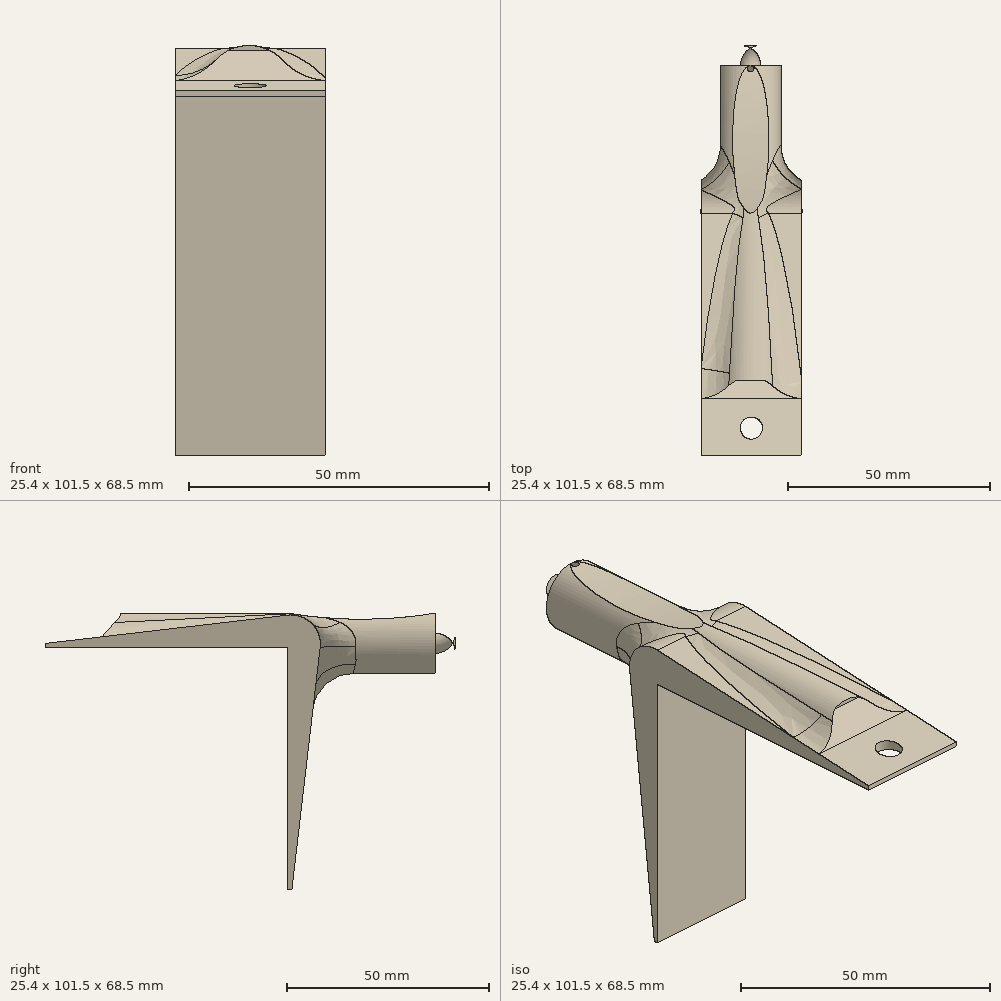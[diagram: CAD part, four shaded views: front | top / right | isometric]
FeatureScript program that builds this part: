
annotation { "Feature Type Name" : "Feature", "Feature Type Description" : "" }
export const myFeature = defineFeature(function(context is Context, id is Id, definition is map)
    precondition{}
    {
        {
            var Q0;
            Q0=qCreatedBy(makeId("Right.planeOp"),FACE);
            var sketch = newSketch(context, id + "F0", { "sketchPlane" : qUnion([Q0])});
            skLineSegment(sketch, "E0", {"start": v(0, 0) * mm, "end": v(0, -60) * mm});
            skLineSegment(sketch, "E1", {"start": v(0, 0) * mm, "end": v(-60, 0) * mm});
            skLineSegment(sketch, "E2", {"start": v(0, 0) * mm, "end": v(0, 8) * mm, "construction": true});
            skLineSegment(sketch, "E3", {"start": v(0, 0) * mm, "end": v(8, 0) * mm, "construction": true});
            skLineSegment(sketch, "E4", {"start": v(-60, 0) * mm, "end": v(-60, 1) * mm});
            skLineSegment(sketch, "E5", {"start": v(0, -60) * mm, "end": v(1, -60) * mm});
            skLineSegment(sketch, "E6", {"start": v(-60, 1) * mm, "end": v(0, 8) * mm});
            skLineSegment(sketch, "E7", {"start": v(8, 0) * mm, "end": v(1, -60) * mm});
            skArc(sketch, "E8", {"start": v(8, 0) * mm, "mid": v(5.94, 5.94) * mm, "end": v(0, 8) * mm});
            skLineSegment(sketch, "E9", {"start": v(-30, 0) * mm, "end": v(0, -30) * mm, "construction": true});
            skSolve(sketch);
        }
        {
            var Q0;
            Q0 = qSketchRegion(id + "F0", true);
            extrude(context, id + "F1", {"entities" : qUnion([Q0]), "depth" : 25 * mm});
        }
        {
            var Q0;
            Q0=qCreatedBy(makeId("Front.planeOp"),FACE);
            var sketch = newSketch(context, id + "F2", { "sketchPlane" : qUnion([Q0])});
            skLineSegment(sketch, "E10.0", {"start": v(25, 0) * mm, "end": v(25, -60) * mm, "construction": true});
            skLineSegment(sketch, "E11", {"start": v(0, 0) * mm, "end": v(25, 0) * mm, "construction": true});
            skCircle(sketch, "E12", {"center": v(12.3, 1) * mm, "radius": 7.5 * mm});
            skLineSegment(sketch, "E13", {"start": v(12.3, 0) * mm, "end": v(12.3, 1) * mm, "construction": true});
            skSolve(sketch);
        }
        {
            var Q0;
            Q0 = qSketchRegion(id + "F2", true);
            extrude(context, id + "F3", {"entities" : qUnion([Q0]), "operationType" : NewBodyOperationType.ADD, "endBound" : BoundingType.SYMMETRIC, "depth" : 83 * mm});
        }
        {
            var Q0;
            Q0=makeQuery(id+"F1.opExtrude","CAP_FACE",FACE,{"disambiguationData":[OSD([sQuery(id+"F0.wireOp",EDGE,"E0"),sQuery(id+"F0.wireOp",EDGE,"E1"),sQuery(id+"F0.wireOp",EDGE,"E4"),sQuery(id+"F0.wireOp",EDGE,"E5"),sQuery(id+"F0.wireOp",EDGE,"E6"),sQuery(id+"F0.wireOp",EDGE,"E7"),sQuery(id+"F0.wireOp",EDGE,"E8")])],"isStart":false});
            var sketch = newSketch(context, id + "F4", { "sketchPlane" : qUnion([Q0])});
            skLineSegment(sketch, "E14.0", {"start": v(0, 0) * mm, "end": v(-60, 0) * mm});
            skLineSegment(sketch, "E15.0", {"start": v(0, 0) * mm, "end": v(0, -60) * mm});
            skLineSegment(sketch, "E16", {"start": v(-60, 0) * mm, "end": v(-60, -60) * mm});
            skLineSegment(sketch, "E17", {"start": v(-60, -60) * mm, "end": v(0, -60) * mm});
            skSolve(sketch);
        }
        {
            var Q0;
            Q0 = qSketchRegion(id + "F4", true);
            var Q1;
            Q1=makeQuery(id+"F1.opExtrude","CAP_FACE",FACE,{"disambiguationData":[OSD([sQuery(id+"F0.wireOp",EDGE,"E0"),sQuery(id+"F0.wireOp",EDGE,"E1"),sQuery(id+"F0.wireOp",EDGE,"E4"),sQuery(id+"F0.wireOp",EDGE,"E5"),sQuery(id+"F0.wireOp",EDGE,"E6"),sQuery(id+"F0.wireOp",EDGE,"E7"),sQuery(id+"F0.wireOp",EDGE,"E8")])],"isStart":true});
            extrude(context, id + "F5", {"entities" : qUnion([Q0]), "operationType" : NewBodyOperationType.REMOVE, "endBound" : BoundingType.UP_TO_SURFACE, "oppositeDirection" : true, "endBoundEntityFace" : qUnion([Q1]), "depth" : 25 * mm});
        }
        {
            var Q0;
            Q0=makeQuery(id+"F3.boolean.opBoolean","INTERSECT",EDGE,{"derivedFrom":[makeQuery(id+"F1.opExtrude","SWEPT_FACE",FACE,{"disambiguationData":[OSD([sQuery(id+"F0.wireOp",EDGE,"E6")])]}),makeQuery(id+"F3.opExtrude","CAP_FACE",FACE,{"disambiguationData":[OSD([sQuery(id+"F2.wireOp",EDGE,"E12")])],"isStart":false})]});
            chamfer(context, id + "F6", {"entities" : qUnion([Q0]), "width" : 5 * mm, "tangentPropagation" : true});
        }
        {
            var Q0;
            Q0=makeQuery(id+"F3.boolean.opBoolean","INTERSECT",EDGE,{"derivedFrom":[makeQuery(id+"F1.opExtrude","SWEPT_FACE",FACE,{"disambiguationData":[OSD([sQuery(id+"F0.wireOp",EDGE,"E7")])]}),makeQuery(id+"F3.opExtrude","SWEPT_FACE",FACE,{"disambiguationData":[OSD([sQuery(id+"F2.wireOp",EDGE,"E12")])]})]});
            fillet(context, id + "F7", {"entities" : qUnion([Q0]), "radius" : 10 * mm, "tangentPropagation" : true, "allowEdgeOverflow" : false});
        }
        {
            var Q0;
            Q0=makeQuery(id+"F3.opExtrude","CAP_EDGE",EDGE,{"disambiguationData":[OSD([sQuery(id+"F2.wireOp",EDGE,"E12")])],"isStart":true});
            fillet(context, id + "F8", {"entities" : qUnion([Q0]), "radius" : 5 * mm, "tangentPropagation" : true, "allowEdgeOverflow" : false});
        }
        {
            var Q0;
            Q0=makeQuery(id+"F1.opExtrude","CAP_FACE",FACE,{"disambiguationData":[OSD([sQuery(id+"F0.wireOp",EDGE,"E0"),sQuery(id+"F0.wireOp",EDGE,"E1"),sQuery(id+"F0.wireOp",EDGE,"E4"),sQuery(id+"F0.wireOp",EDGE,"E5"),sQuery(id+"F0.wireOp",EDGE,"E6"),sQuery(id+"F0.wireOp",EDGE,"E7"),sQuery(id+"F0.wireOp",EDGE,"E8")])],"isStart":false});
            var sketch = newSketch(context, id + "F9", { "sketchPlane" : qUnion([Q0])});
            skLineSegment(sketch, "E18.0", {"start": v(36.5, -6.5) * mm, "end": v(36.5, 8.5) * mm, "construction": true});
            skLineSegment(sketch, "E19", {"start": v(0, 0) * mm, "end": v(0, 8.5) * mm, "construction": true});
            skLineSegment(sketch, "E20", {"start": v(0, 8.5) * mm, "end": v(36.5, 8.5) * mm});
            skArc(sketch, "E21", {"start": v(0, 8.5) * mm, "mid": v(18.25, 7) * mm, "end": v(36.5, 8.5) * mm});
            skLineSegment(sketch, "E22", {"start": v(18.25, 7) * mm, "end": v(18.25, 8.5) * mm, "construction": true});
            skSolve(sketch);
        }
        {
            var Q0;
            Q0 = qSketchRegion(id + "F9", true);
            var Q1;
            Q1=makeQuery(id+"F1.opExtrude","CAP_FACE",FACE,{"disambiguationData":[OSD([sQuery(id+"F0.wireOp",EDGE,"E0"),sQuery(id+"F0.wireOp",EDGE,"E1"),sQuery(id+"F0.wireOp",EDGE,"E4"),sQuery(id+"F0.wireOp",EDGE,"E5"),sQuery(id+"F0.wireOp",EDGE,"E6"),sQuery(id+"F0.wireOp",EDGE,"E7"),sQuery(id+"F0.wireOp",EDGE,"E8")])],"isStart":true});
            extrude(context, id + "F10", {"entities" : qUnion([Q0]), "operationType" : NewBodyOperationType.REMOVE, "endBound" : BoundingType.UP_TO_SURFACE, "oppositeDirection" : true, "endBoundEntityFace" : qUnion([Q1]), "depth" : 25 * mm});
        }
        {
            var Q0;
            Q0=qCreatedBy(makeId("Top.planeOp"),FACE);
            var sketch = newSketch(context, id + "F11", { "sketchPlane" : qUnion([Q0])});
            skLineSegment(sketch, "E23.0.0", {"start": v(25, -46.47) * mm, "end": v(0, -46.47) * mm, "construction": true});
            skLineSegment(sketch, "E23.0.1", {"start": v(0, -46.47) * mm, "end": v(0, -60) * mm, "construction": true});
            skLineSegment(sketch, "E23.0.2", {"start": v(0, -60) * mm, "end": v(25, -60) * mm, "construction": true});
            skLineSegment(sketch, "E23.0.3", {"start": v(25, -60) * mm, "end": v(25, -46.47) * mm, "construction": true});
            skLineSegment(sketch, "E24", {"start": v(0, -53.23) * mm, "end": v(25, -53.23) * mm, "construction": true});
            skLineSegment(sketch, "E25", {"start": v(12.5, -46.47) * mm, "end": v(12.5, -60) * mm, "construction": true});
            skCircle(sketch, "E26", {"center": v(12.5, -53.23) * mm, "radius": 2.75 * mm});
            skSolve(sketch);
        }
        {
            var Q0;
            Q0 = qSketchRegion(id + "F11", true);
            extrude(context, id + "F12", {"entities" : qUnion([Q0]), "operationType" : NewBodyOperationType.REMOVE, "depth" : 25 * mm});
        }
    });
